# Revit family: PHBH-latest
name_source: partatom
category: Lighting Fixtures
revit_build: Autodesk Revit 2014 (Build: 20130308_1515(x64)
units: mm (PartAtom-declared; Revit-internal decimal feet)

## types (1)
- PHBH-latest
    Applications = Commercial Indoor
Industrial
Warehouse
Heavy Industry
Light Industry
Petroleum
Chemical/Plastic
Paper/Textile
Iron/Steel
    Certifications = UL,UL1598,UL1598A,CSA
    Color Filter = 16777215
    Default Elevation = 48"
    Description = The Performance High Bay is the new standard for industrial lighting. A well sealed die cast housing coupled with a choice of four optics results in a durable, rugged high bay for those tough industrial applications.
    Dimming Lamp Color Temperature Shift = <None>
    Emit Shape Visible in Rendering = No
    Emit from Circle Diameter = 18"
    Features = Class I, Div II, Groups A, B, C and D
Three piece low copper alloy die cast aluminum housing
Easy one person installation on threaded conduit (¾" or 1")
60,000 hour LEDs at L80 (up to 86,000 projected life) for reduced maintenance
Weight: 30 lbs
Up to 28,000 lumens
Up to 141 LPW (lumens/watt)
Five lens options:High transmissive flat acrylicTranslucent sag polycarbonatePrismatic drop acrylicConical drop acrylicFlat clear glass
Replacement for 400W, 250W, or 175W
Standard unit is continuously dimmable
Mid power LEDs for high LPW and low glare
Universal voltage of 120VAC - 277VAC/50/60 Hz
Ambient temperature range is from -40°C to 65°C
347 VAC / 480 VAC 50/60 Hz
    Finish = Paint - Hubbell - White Texture
    IP Rating = IP66
    Manufacturer = Hubbell Industrial Lighting
    Model = PHBH
    Opal lens = Hubbell - White Glass
    Photometric Web File = PHBH-3K-LV-CDL.ies
    Product Doucmentaion Link = https://hubbellcdn.com
    Product Link = https://www.hubbell.com
    Tilt Angle = 90.00°
    URL = www.hubbellindustrial.com
    Warranty = 5 year Warranty

## geometry (parser evidence)
native form markers: Sweep x5
no freeform markers — native parametric forms only
